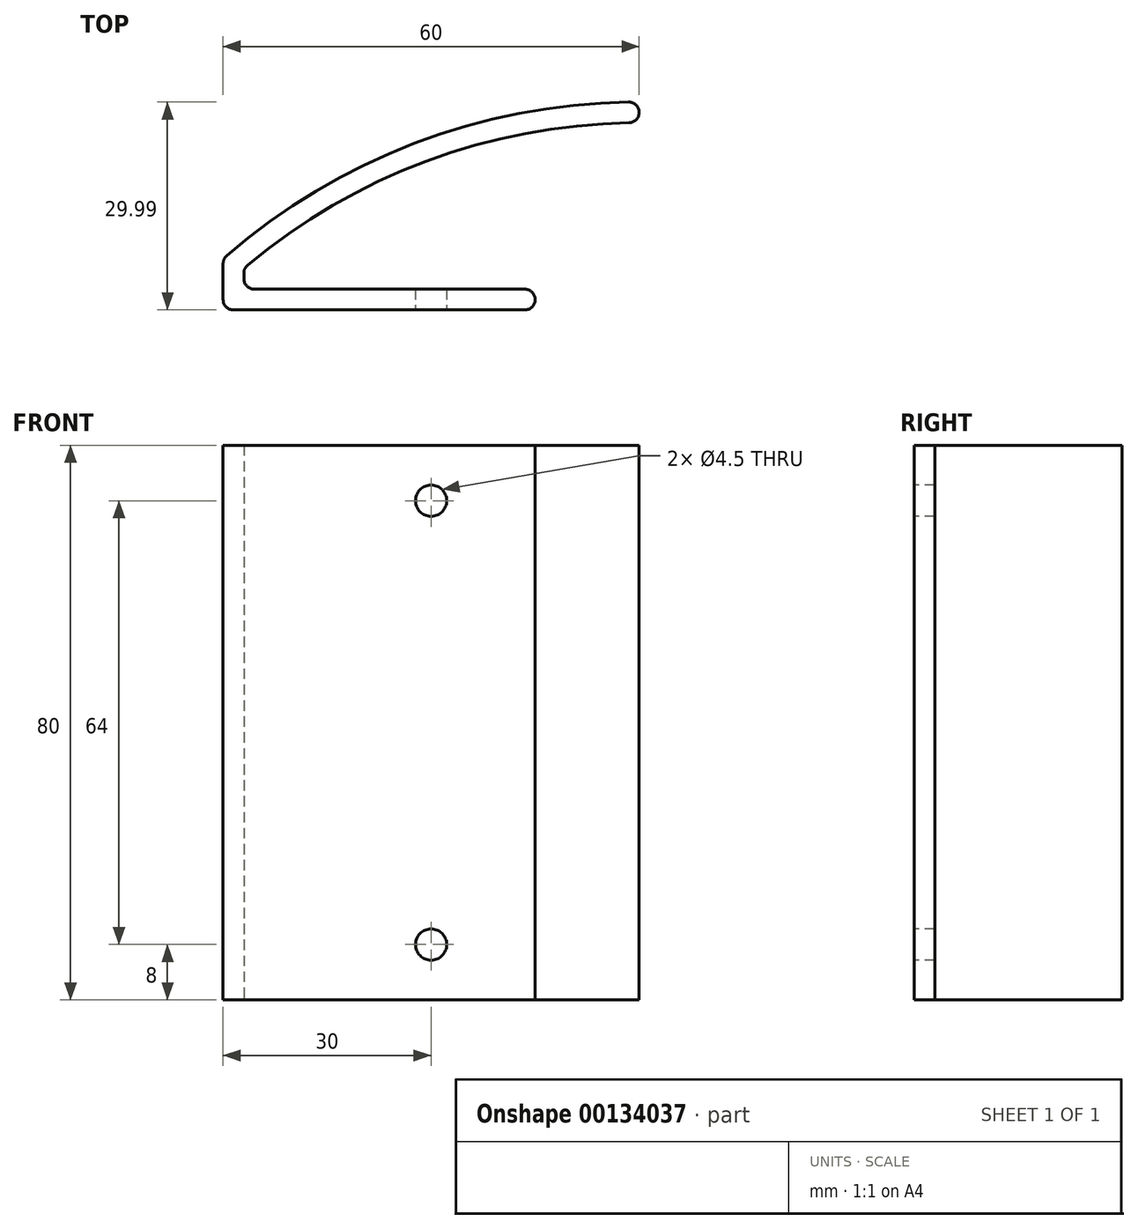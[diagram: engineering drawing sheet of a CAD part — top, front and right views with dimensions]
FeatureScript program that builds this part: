
annotation { "Feature Type Name" : "Feature", "Feature Type Description" : "" }
export const myFeature = defineFeature(function(context is Context, id is Id, definition is map)
    precondition{}
    {
        {
            var Q0;
            Q0=qCreatedBy(makeId("Top.planeOp"),FACE);
            var sketch = newSketch(context, id + "F0", { "sketchPlane" : qUnion([Q0])});
            skLineSegment(sketch, "E0", {"start": v(3, 3) * mm, "end": v(45, 3) * mm});
            skLineSegment(sketch, "E1", {"start": v(45, 3) * mm, "end": v(45, 0) * mm});
            skLineSegment(sketch, "E2", {"start": v(45, 0) * mm, "end": v(0, 0) * mm});
            skLineSegment(sketch, "E3", {"start": v(3, 3) * mm, "end": v(3, 6) * mm});
            skLineSegment(sketch, "E4", {"start": v(0, 0) * mm, "end": v(0, 7.37) * mm});
            skArc(sketch, "E5", {"start": v(60, 27) * mm, "mid": v(29.63, 21.58) * mm, "end": v(3, 6) * mm});
            skLineSegment(sketch, "E6", {"start": v(60, 27) * mm, "end": v(60, 30) * mm});
            skArc(sketch, "E7", {"start": v(60, 30) * mm, "mid": v(27.94, 24.15) * mm, "end": v(0, 7.37) * mm});
            skSolve(sketch);
        }
        {
            var Q0;
            Q0=makeQuery(id+"F0.imprint","IMPRINT",FACE,{"disambiguationData":[TD([[makeQuery(id+"F0.imprint","IMPRINT",EDGE,{"derivedFrom":sQuery(id+"F0.wireOp",EDGE,"aJll9afi-40ZR-fted-he3V-BIla2pT1cnQ4")}),-1.0]])]});
            var Q1;
            Q1=makeQuery(id+"F0.imprint","IMPRINT",FACE,{"disambiguationData":[TD([[makeQuery(id+"F0.imprint","IMPRINT",EDGE,{"derivedFrom":sQuery(id+"F0.wireOp",EDGE,"E0")}),-1.0]])]});
            extrude(context, id + "F1", {"entities" : qUnion([Q0, Q1]), "depth" : 80 * mm});
        }
        {
            var Q0;
            Q0=makeQuery(id+"F1.opExtrude","SWEPT_FACE",FACE,{"disambiguationData":[OSD([sQuery(id+"F0.wireOp",EDGE,"E2")])]});
            var sketch = newSketch(context, id + "F2", { "sketchPlane" : qUnion([Q0])});
            skCircle(sketch, "E8", {"center": v(30, 72) * mm, "radius": 2.25 * mm});
            skCircle(sketch, "E9", {"center": v(30, 8) * mm, "radius": 2.25 * mm});
            skLineSegment(sketch, "E10", {"start": v(30, 72) * mm, "end": v(0, 80) * mm, "construction": true});
            skLineSegment(sketch, "E11", {"start": v(30, 8) * mm, "end": v(0, 0) * mm, "construction": true});
            skLineSegment(sketch, "E12", {"start": v(30, 72) * mm, "end": v(30, 8) * mm, "construction": true});
            skSolve(sketch);
        }
        {
            var Q0;
            Q0 = qSketchRegion(id + "F2", true);
            var Q1;
            Q1=makeQuery(id+"F1.opExtrude","SWEPT_FACE",FACE,{"disambiguationData":[OSD([sQuery(id+"F0.wireOp",EDGE,"E0")])]});
            extrude(context, id + "F3", {"entities" : qUnion([Q0]), "operationType" : NewBodyOperationType.REMOVE, "endBound" : BoundingType.UP_TO_SURFACE, "oppositeDirection" : true, "endBoundEntityFace" : qUnion([Q1]), "depth" : 25 * mm});
        }
        {
            var Q0;
            Q0=makeQuery(id+"F1.opExtrude","SWEPT_EDGE",EDGE,{"disambiguationData":[OSD([sQuery(id+"F0.wireOp",EDGE,"E1"),sQuery(id+"F0.wireOp",EDGE,"E2")])]});
            var Q1;
            Q1=makeQuery(id+"F1.opExtrude","SWEPT_EDGE",EDGE,{"disambiguationData":[OSD([sQuery(id+"F0.wireOp",EDGE,"E0"),sQuery(id+"F0.wireOp",EDGE,"E1")])]});
            var Q2;
            Q2=makeQuery(id+"F1.opExtrude","SWEPT_EDGE",EDGE,{"disambiguationData":[OSD([sQuery(id+"F0.wireOp",EDGE,"E2"),sQuery(id+"F0.wireOp",EDGE,"E4")])]});
            var Q3;
            Q3=makeQuery(id+"F1.opExtrude","SWEPT_EDGE",EDGE,{"disambiguationData":[OSD([sQuery(id+"F0.wireOp",EDGE,"E4"),sQuery(id+"F0.wireOp",EDGE,"E7")])]});
            var Q4;
            Q4=makeQuery(id+"F1.opExtrude","SWEPT_EDGE",EDGE,{"disambiguationData":[OSD([sQuery(id+"F0.wireOp",EDGE,"E6"),sQuery(id+"F0.wireOp",EDGE,"E7")])]});
            var Q5;
            Q5=makeQuery(id+"F1.opExtrude","SWEPT_EDGE",EDGE,{"disambiguationData":[OSD([sQuery(id+"F0.wireOp",EDGE,"E5"),sQuery(id+"F0.wireOp",EDGE,"E6")])]});
            var Q6;
            Q6=makeQuery(id+"F1.opExtrude","SWEPT_EDGE",EDGE,{"disambiguationData":[OSD([sQuery(id+"F0.wireOp",EDGE,"E0"),sQuery(id+"F0.wireOp",EDGE,"E3")])]});
            var Q7;
            Q7=makeQuery(id+"F1.opExtrude","SWEPT_EDGE",EDGE,{"disambiguationData":[OSD([sQuery(id+"F0.wireOp",EDGE,"E3"),sQuery(id+"F0.wireOp",EDGE,"E5")])]});
            fillet(context, id + "F4", {"entities" : qUnion([Q0, Q1, Q2, Q3, Q4, Q5, Q6, Q7]), "radius" : 1.5 * mm, "tangentPropagation" : true, "allowEdgeOverflow" : false});
        }
    });
